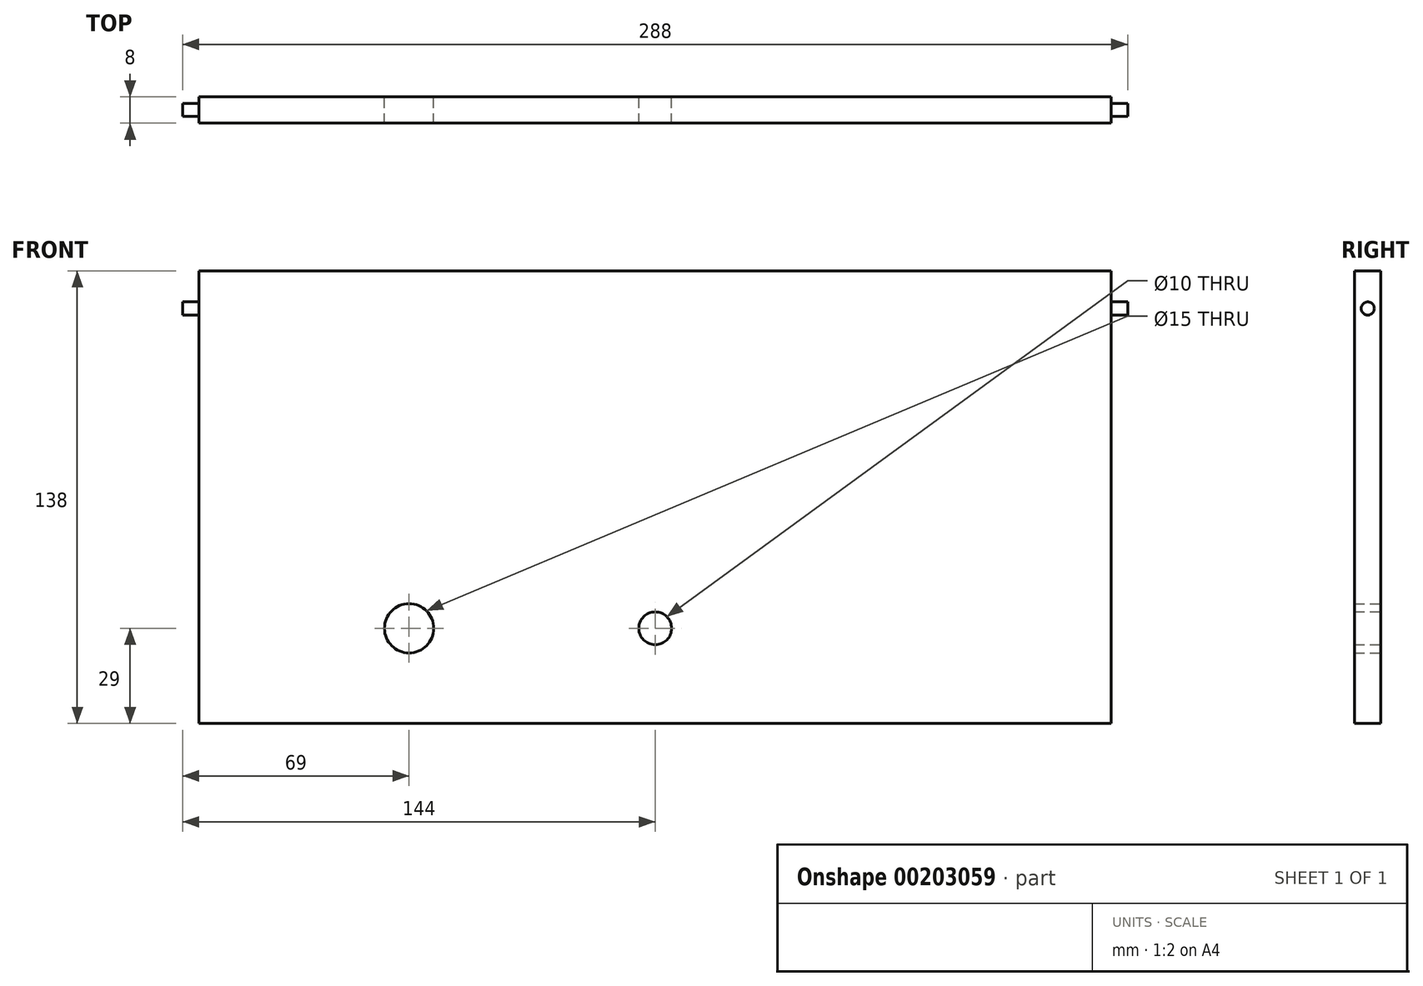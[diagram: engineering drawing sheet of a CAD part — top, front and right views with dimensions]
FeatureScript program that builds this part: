
annotation { "Feature Type Name" : "Feature", "Feature Type Description" : "" }
export const myFeature = defineFeature(function(context is Context, id is Id, definition is map)
    precondition{}
    {
        {
            var Q0;
            Q0=qCreatedBy(makeId("Front.planeOp"),FACE);
            var sketch = newSketch(context, id + "F0", { "sketchPlane" : qUnion([Q0])});
            skLineSegment(sketch, "E0.bottom", {"start": v(139, -69) * mm, "end": v(-139, -69) * mm});
            skLineSegment(sketch, "E0.top", {"start": v(139, 69) * mm, "end": v(-139, 69) * mm});
            skLineSegment(sketch, "E0.left", {"start": v(139, -69) * mm, "end": v(139, 69) * mm});
            skLineSegment(sketch, "E0.right", {"start": v(-139, -69) * mm, "end": v(-139, 69) * mm});
            skPoint(sketch, "E0.middle", {"position": v(0, 0) * mm});
            skLineSegment(sketch, "E1", {"start": v(0, 126.55) * mm, "end": v(0, -96.37) * mm, "construction": true});
            skPoint(sketch, "E1.endSnap0", {"position": v(0, -69) * mm});
            skLineSegment(sketch, "E2", {"start": v(-158.16, 0) * mm, "end": v(154.51, 0) * mm, "construction": true});
            skCircle(sketch, "E3", {"center": v(0, -40) * mm, "radius": 5 * mm});
            skCircle(sketch, "E4", {"center": v(-75, -40) * mm, "radius": 7.5 * mm});
            skSolve(sketch);
        }
        {
            var Q0;
            Q0 = qSketchRegion(id + "F0", true);
            extrude(context, id + "F1", {"entities" : qUnion([Q0]), "depth" : 8 * mm});
        }
        {
            var Q0;
            Q0=makeQuery(id+"F1.opExtrude","SWEPT_FACE",FACE,{"disambiguationData":[OSD([sQuery(id+"F0.wireOp",EDGE,"E0.left")])]});
            var sketch = newSketch(context, id + "F2", { "sketchPlane" : qUnion([Q0])});
            skLineSegment(sketch, "E5.0", {"start": v(0, -69) * mm, "end": v(0, 69) * mm, "construction": true});
            skLineSegment(sketch, "E5.1", {"start": v(-8, -69) * mm, "end": v(-8, 69) * mm, "construction": true});
            skLineSegment(sketch, "E5.2", {"start": v(-8, 69) * mm, "end": v(0, 69) * mm, "construction": true});
            skLineSegment(sketch, "E5.3", {"start": v(-8, -69) * mm, "end": v(0, -69) * mm, "construction": true});
            skLineSegment(sketch, "E6", {"start": v(-4, 69) * mm, "end": v(-4, 57.5) * mm, "construction": true});
            skCircle(sketch, "E7", {"center": v(-4, 57.5) * mm, "radius": 2 * mm});
            skSolve(sketch);
        }
        {
            var Q0;
            Q0 = qSketchRegion(id + "F2", true);
            extrude(context, id + "F3", {"entities" : qUnion([Q0]), "depth" : 5 * mm});
        }
        {
            var Q0;
            Q0=makeQuery(id+"F3.opExtrude","SWEPT_BODY",BODY,{"disambiguationData":[OSD([sQuery(id+"F2.wireOp",EDGE,"E7")])]});
            var Q1;
            Q1=qCreatedBy(makeId("Right.planeOp"),FACE);
            mirror(context, id + "F4", {"operationType" : NewBodyOperationType.ADD, "entities" : qUnion([Q0]), "mirrorPlane" : qUnion([Q1])});
        }
    });
